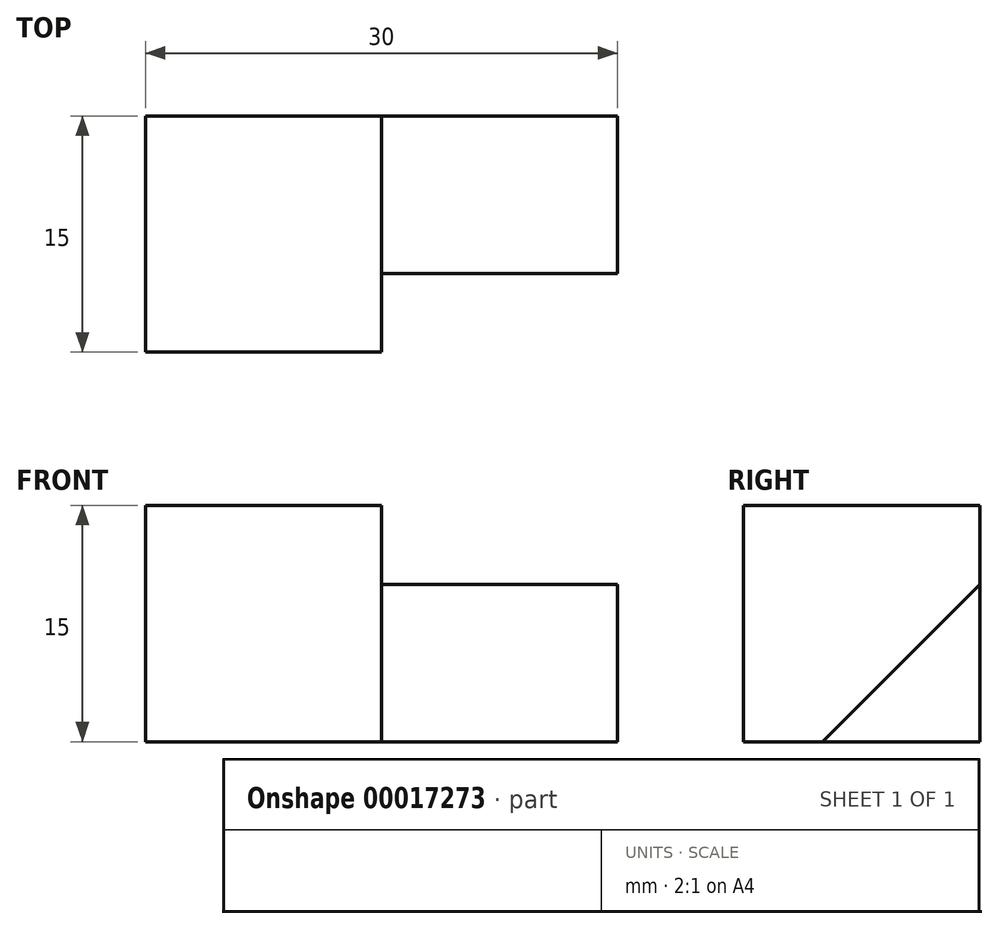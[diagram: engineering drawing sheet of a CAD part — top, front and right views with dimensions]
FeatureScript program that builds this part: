
annotation { "Feature Type Name" : "Feature", "Feature Type Description" : "" }
export const myFeature = defineFeature(function(context is Context, id is Id, definition is map)
    precondition{}
    {
        {
            var Q0;
            Q0=qCreatedBy(makeId("Front.planeOp"),FACE);
            var sketch = newSketch(context, id + "F0", { "sketchPlane" : qUnion([Q0])});
            skLineSegment(sketch, "E0.bottom", {"start": v(-25.84, 18.75) * mm, "end": v(-10.84, 18.75) * mm});
            skLineSegment(sketch, "E0.top", {"start": v(-25.84, 3.75) * mm, "end": v(-10.84, 3.75) * mm});
            skLineSegment(sketch, "E0.left", {"start": v(-25.84, 18.75) * mm, "end": v(-25.84, 3.75) * mm});
            skLineSegment(sketch, "E0.right", {"start": v(-10.84, 18.75) * mm, "end": v(-10.84, 3.75) * mm});
            skSolve(sketch);
        }
        {
            var Q0;
            Q0 = qSketchRegion(id + "F0", true);
            extrude(context, id + "F1", {"entities" : qUnion([Q0]), "depth" : 15 * mm});
        }
        {
            var Q0;
            Q0=makeQuery(id+"F1.opExtrude","SWEPT_FACE",FACE,{"disambiguationData":[OSD([sQuery(id+"F0.wireOp",EDGE,"E0.right")])]});
            var sketch = newSketch(context, id + "F2", { "sketchPlane" : qUnion([Q0])});
            skLineSegment(sketch, "E1", {"start": v(-10, 3.75) * mm, "end": v(0, 13.75) * mm});
            skLineSegment(sketch, "E2", {"start": v(0, 13.75) * mm, "end": v(0, 3.75) * mm});
            skLineSegment(sketch, "E3", {"start": v(0, 3.75) * mm, "end": v(-10, 3.75) * mm});
            skSolve(sketch);
        }
        {
            var Q0;
            Q0 = qSketchRegion(id + "F2", true);
            extrude(context, id + "F3", {"entities" : qUnion([Q0]), "operationType" : NewBodyOperationType.ADD, "depth" : 15 * mm});
        }
    });
